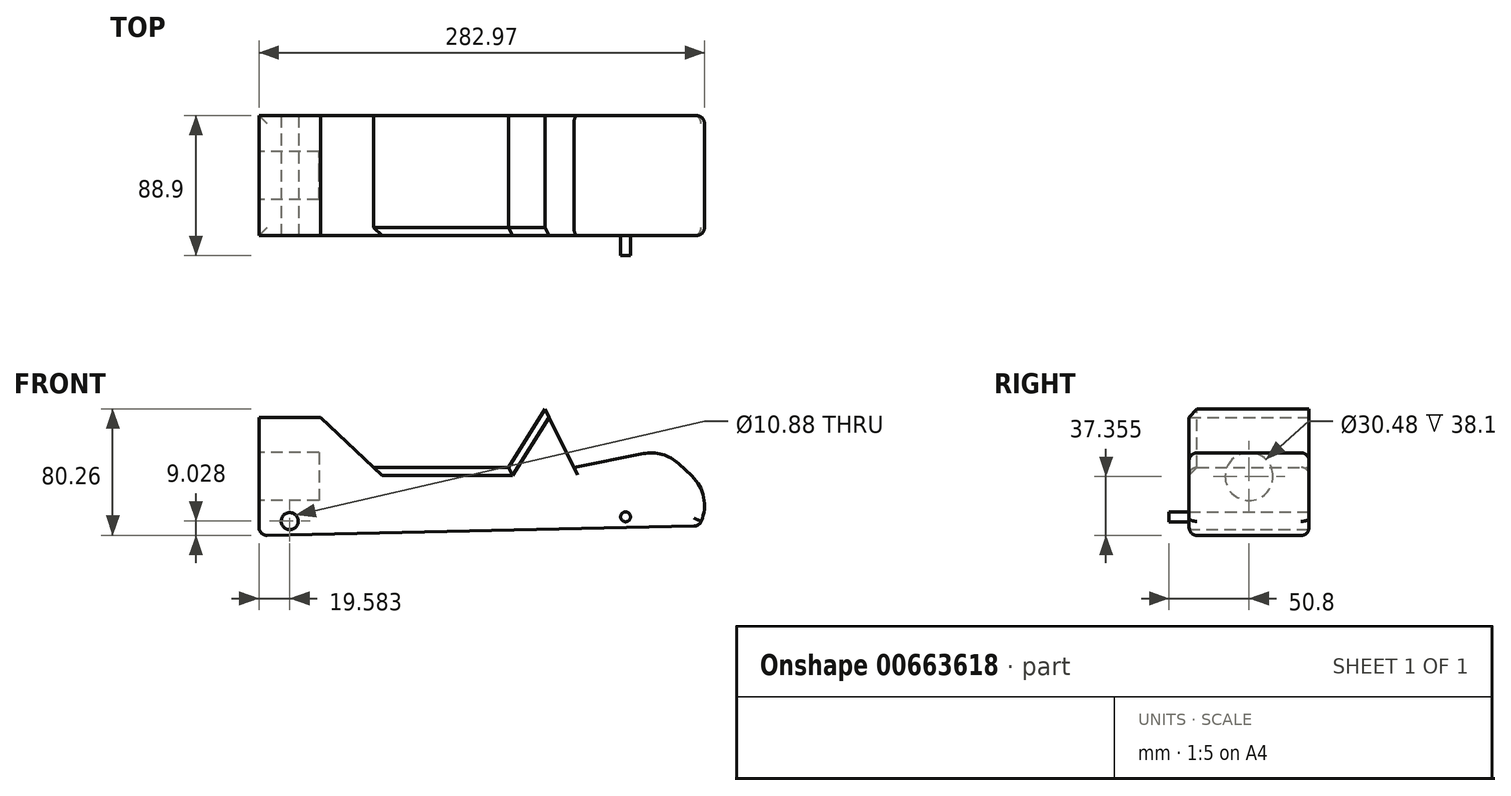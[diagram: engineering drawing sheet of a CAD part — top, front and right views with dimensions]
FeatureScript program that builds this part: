
annotation { "Feature Type Name" : "Feature", "Feature Type Description" : "" }
export const myFeature = defineFeature(function(context is Context, id is Id, definition is map)
    precondition{}
    {
        {
            var Q0;
            Q0=qCreatedBy(makeId("Front.planeOp"),FACE);
            var sketch = newSketch(context, id + "F0", { "sketchPlane" : qUnion([Q0])});
            skLineSegment(sketch, "E0", {"start": v(78.5, 0) * mm, "end": v(357.84, 6.04) * mm});
            skLineSegment(sketch, "E1", {"start": v(78.5, 0) * mm, "end": v(78.5, 74.93) * mm});
            skLineSegment(sketch, "E2", {"start": v(78.5, 74.93) * mm, "end": v(117.64, 74.93) * mm});
            skLineSegment(sketch, "E3", {"start": v(117.64, 74.93) * mm, "end": v(151.45, 43.26) * mm});
            skLineSegment(sketch, "E4", {"start": v(151.45, 43.26) * mm, "end": v(236.9, 43.26) * mm});
            skLineSegment(sketch, "E5", {"start": v(236.9, 43.26) * mm, "end": v(260.1, 80.37) * mm});
            skLineSegment(sketch, "E6", {"start": v(260.1, 80.37) * mm, "end": v(278.52, 43.26) * mm});
            skLineSegment(sketch, "E7", {"start": v(278.52, 43.26) * mm, "end": v(322.64, 52.03) * mm});
            skLineSegment(sketch, "E8", {"start": v(344.95, 45.65) * mm, "end": v(353.44, 37.7) * mm});
            skLineSegment(sketch, "E9", {"start": v(358.25, 6.78) * mm, "end": v(357.84, 6.04) * mm});
            skPoint(sketch, "E10.visualSharp", {"position": v(367.94, 24.12) * mm});
            skArc(sketch, "E10.filletArc", {"start": v(358.25, 6.78) * mm, "mid": v(361.18, 23.07) * mm, "end": v(353.44, 37.7) * mm});
            skPoint(sketch, "E11.visualSharp", {"position": v(335.43, 54.57) * mm});
            skArc(sketch, "E11.filletArc", {"start": v(344.95, 45.65) * mm, "mid": v(334.57, 51.54) * mm, "end": v(322.64, 52.03) * mm});
            skSolve(sketch);
        }
        {
            var Q0;
            Q0 = qSketchRegion(id + "F0", true);
            extrude(context, id + "F1", {"entities" : qUnion([Q0]), "depth" : 50.8 * mm, "offsetDistance" : 25.4 * mm});
        }
        {
            var Q0;
            Q0 = qSketchRegion(id + "F0", true);
            extrude(context, id + "F2", {"entities" : qUnion([Q0]), "operationType" : NewBodyOperationType.ADD, "depth" : 76.2 * mm, "offsetDistance" : 25.4 * mm});
        }
        {
            var Q0;
            {var subQ0=sQuery(id+"F0.wireOp",EDGE,"E1");Q0=makeQuery(id+"F2.boolean.opBoolean","MERGE",FACE,{"derivedFrom":[makeQuery(id+"F1.opExtrude","SWEPT_FACE",FACE,{"disambiguationData":[OSD([subQ0])]}),makeQuery(id+"F2.opExtrude","SWEPT_FACE",FACE,{"disambiguationData":[OSD([subQ0])]})]});}
            var sketch = newSketch(context, id + "F3", { "sketchPlane" : qUnion([Q0])});
            skCircle(sketch, "E12", {"center": v(38.1, 37.47) * mm, "radius": 15.24 * mm});
            skPoint(sketch, "E12.centerSnap0", {"position": v(38.1, 0) * mm});
            skPoint(sketch, "E12.centerSnap1", {"position": v(0, 37.47) * mm});
            skSolve(sketch);
        }
        {
            var Q0;
            Q0 = qSketchRegion(id + "F3", true);
            extrude(context, id + "F4", {"entities" : qUnion([Q0]), "operationType" : NewBodyOperationType.REMOVE, "oppositeDirection" : true, "depth" : 38.1 * mm, "offsetDistance" : 25.4 * mm});
        }
        {
            var Q0;
            Q0=makeQuery(id+"F2.opExtrude","CAP_FACE",FACE,{"disambiguationData":[OSD([sQuery(id+"F0.wireOp",EDGE,"E0"),sQuery(id+"F0.wireOp",EDGE,"E1"),sQuery(id+"F0.wireOp",EDGE,"E2"),sQuery(id+"F0.wireOp",EDGE,"E3"),sQuery(id+"F0.wireOp",EDGE,"E4"),sQuery(id+"F0.wireOp",EDGE,"E5"),sQuery(id+"F0.wireOp",EDGE,"E6"),sQuery(id+"F0.wireOp",EDGE,"E7"),sQuery(id+"F0.wireOp",EDGE,"E8"),sQuery(id+"F0.wireOp",EDGE,"E9"),sQuery(id+"F0.wireOp",EDGE,"E10.filletArc"),sQuery(id+"F0.wireOp",EDGE,"E11.filletArc")])],"isStart":false});
            var sketch = newSketch(context, id + "F5", { "sketchPlane" : qUnion([Q0])});
            skCircle(sketch, "E13", {"center": v(98.1, 9.14) * mm, "radius": 5.44 * mm});
            skSolve(sketch);
        }
        {
            var Q0;
            Q0 = qSketchRegion(id + "F5", true);
            extrude(context, id + "F6", {"entities" : qUnion([Q0]), "operationType" : NewBodyOperationType.REMOVE, "oppositeDirection" : true, "depth" : 254 * mm, "offsetDistance" : 25.4 * mm});
        }
        {
            var Q0;
            Q0=makeQuery(id+"F2.opExtrude","CAP_FACE",FACE,{"disambiguationData":[OSD([sQuery(id+"F0.wireOp",EDGE,"E0"),sQuery(id+"F0.wireOp",EDGE,"E1"),sQuery(id+"F0.wireOp",EDGE,"E2"),sQuery(id+"F0.wireOp",EDGE,"E3"),sQuery(id+"F0.wireOp",EDGE,"E4"),sQuery(id+"F0.wireOp",EDGE,"E5"),sQuery(id+"F0.wireOp",EDGE,"E6"),sQuery(id+"F0.wireOp",EDGE,"E7"),sQuery(id+"F0.wireOp",EDGE,"E8"),sQuery(id+"F0.wireOp",EDGE,"E9"),sQuery(id+"F0.wireOp",EDGE,"E10.filletArc"),sQuery(id+"F0.wireOp",EDGE,"E11.filletArc")])],"isStart":false});
            var sketch = newSketch(context, id + "F7", { "sketchPlane" : qUnion([Q0])});
            skCircle(sketch, "E14", {"center": v(311.36, 11.89) * mm, "radius": 3.11 * mm});
            skSolve(sketch);
        }
        {
            var Q0;
            Q0 = qSketchRegion(id + "F7", true);
            extrude(context, id + "F8", {"entities" : qUnion([Q0]), "depth" : 12.7 * mm, "offsetDistance" : 25.4 * mm});
        }
        {
            var Q0;
            {var subQ0=sQuery(id+"F0.wireOp",EDGE,"E11.filletArc");Q0=makeQuery(id+"F2.boolean.opBoolean","MERGE",FACE,{"derivedFrom":[makeQuery(id+"F1.opExtrude","SWEPT_FACE",FACE,{"disambiguationData":[OSD([subQ0])]}),makeQuery(id+"F2.opExtrude","SWEPT_FACE",FACE,{"disambiguationData":[OSD([subQ0])]})]});}
            var Q1;
            {var subQ0=sQuery(id+"F0.wireOp",EDGE,"E8");Q1=makeQuery(id+"F2.boolean.opBoolean","MERGE",FACE,{"derivedFrom":[makeQuery(id+"F1.opExtrude","SWEPT_FACE",FACE,{"disambiguationData":[OSD([subQ0])]}),makeQuery(id+"F2.opExtrude","SWEPT_FACE",FACE,{"disambiguationData":[OSD([subQ0])]})]});}
            fillet(context, id + "F9", {"entities" : qUnion([Q0, Q1]), "radius" : 5.08 * mm, "tangentPropagation" : true, "allowEdgeOverflow" : false});
        }
        {
            var Q0;
            {var subQ0=sQuery(id+"F0.wireOp",EDGE,"E10.filletArc");Q0=makeQuery(id+"F2.boolean.opBoolean","MERGE",FACE,{"derivedFrom":[makeQuery(id+"F1.opExtrude","SWEPT_FACE",FACE,{"disambiguationData":[OSD([subQ0])]}),makeQuery(id+"F2.opExtrude","SWEPT_FACE",FACE,{"disambiguationData":[OSD([subQ0])]})]});}
            var Q1;
            {var subQ0=sQuery(id+"F0.wireOp",EDGE,"E0");Q1=makeQuery(id+"F2.boolean.opBoolean","MERGE",FACE,{"derivedFrom":[makeQuery(id+"F1.opExtrude","SWEPT_FACE",FACE,{"disambiguationData":[OSD([subQ0])]}),makeQuery(id+"F2.opExtrude","SWEPT_FACE",FACE,{"disambiguationData":[OSD([subQ0])]})]});}
            fillet(context, id + "F10", {"entities" : qUnion([Q0, Q1]), "radius" : 5.08 * mm, "tangentPropagation" : true, "allowEdgeOverflow" : false});
        }
        {
            var Q0;
            Q0=makeQuery(id+"F2.opExtrude","CAP_EDGE",EDGE,{"disambiguationData":[OSD([sQuery(id+"F0.wireOp",EDGE,"E5")])],"isStart":false});
            var Q1;
            Q1=makeQuery(id+"F2.opExtrude","CAP_EDGE",EDGE,{"disambiguationData":[OSD([sQuery(id+"F0.wireOp",EDGE,"E4")])],"isStart":false});
            chamfer(context, id + "F11", {"entities" : qUnion([Q0, Q1]), "width" : 5.08 * mm, "tangentPropagation" : true});
        }
    });
